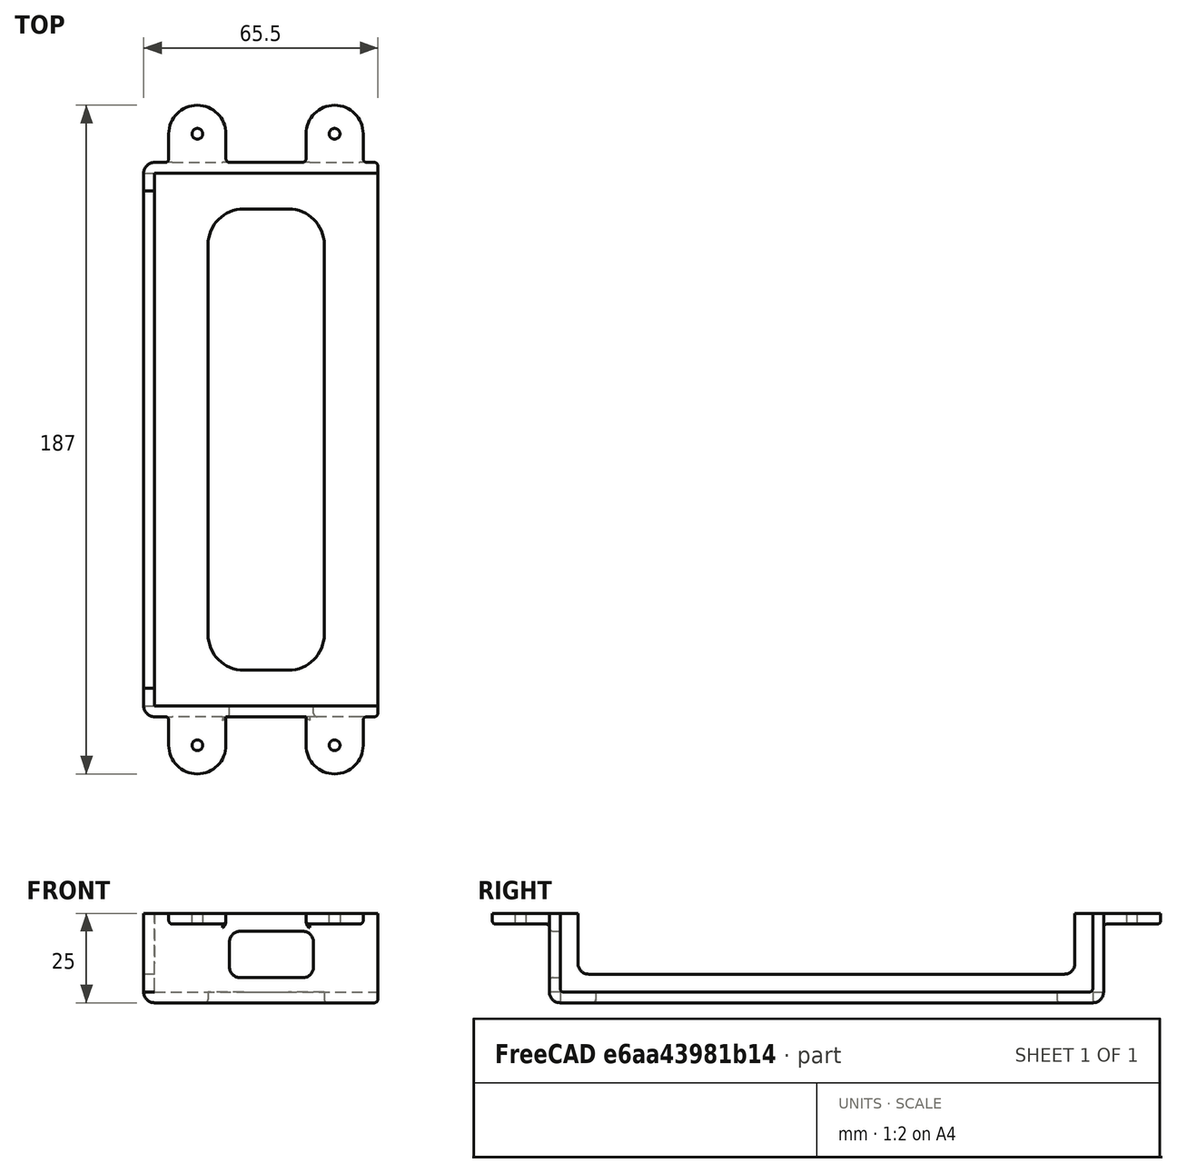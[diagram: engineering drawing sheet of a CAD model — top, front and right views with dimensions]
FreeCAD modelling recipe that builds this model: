
FCSTD DOCUMENT  (FreeCAD 0.21R33668 +7 (Git))
Label: UnderTableBracket-3
License: All rights reserved
LicenseURL: http://en.wikipedia.org/wiki/All_rights_reserved
objects: Sketcher::SketchObject×4, PartDesign::Pocket×3, PartDesign::Fillet×2, Spreadsheet::Sheet×1, PartDesign::AdditiveBox×1, PartDesign::Thickness×1, PartDesign::Pad×1, PartDesign::LinearPattern×1, PartDesign::Plane×1, PartDesign::Mirrored×1, PartDesign::MultiTransform×1, PartDesign::Body×1, App::Part×1, Mesh::Feature×1
note: 25 computed .brp shape members not serialized (recipe doc carries the construction recipe); baked Part::Feature solids carry a one-line shape summary decoded from their .brp

FEATURE [Spreadsheet::Sheet] Spreadsheet
  cells = A1='Width; B1(Width)=149; A2='Height; B2(Height)=22; A3='Depth; B3(Depth)=62.5; A4='Screw Diameter; B4(ScrewDiameter)=3
FEATURE [PartDesign::AdditiveBox] Box
  AttacherType = Attacher::AttachEngine3D
  Height = 22
  Length = 62.5
  Width = 149
  expr: Height = Spreadsheet.Height
  expr: Length = Spreadsheet.Depth
  expr: Width = Spreadsheet.Width
FEATURE [PartDesign::Thickness] Thickness
  Base = -> Box [Face6,Face2]
  BaseFeature = -> Box
  Intersection = false
  Join = 0
  Mode = 0
  SupportTransform = false
  Value = 3
FEATURE [Sketcher::SketchObject] Sketch
  ExternalGeometry = -> [Thickness]
  FullyConstrained = false
  MapMode = 5
  Placement = pos=(0,0,0) rot=(0.57735,0.57735,0.57735;2.0944rad)
  Support = -> [Thickness]
  sketch-geometry (8):
    g0: LineSegment StartX=144 StartY=22 StartZ=0 EndX=144 EndY=8 EndZ=0
    g1: ArcOfCircle CenterX=141 CenterY=8 CenterZ=0 NormalX=0 NormalY=0 NormalZ=1 AngleXU=0 Radius=3 StartAngle=4.71239 EndAngle=6.28319
    g2: LineSegment StartX=141 StartY=5 StartZ=0 EndX=8 EndY=5 EndZ=0
    g3: ArcOfCircle CenterX=8 CenterY=8 CenterZ=0 NormalX=0 NormalY=0 NormalZ=1 AngleXU=0 Radius=3 StartAngle=3.14159 EndAngle=4.71239
    g4: LineSegment StartX=5 StartY=8 StartZ=0 EndX=5 EndY=22 EndZ=0
    g5: GeomPoint X=5 Y=35.516 Z=0
    g6: GeomPoint X=144 Y=5 Z=0
    g7: LineSegment StartX=5 StartY=22 StartZ=0 EndX=144 EndY=22 EndZ=0
  constraints (19):
    c: Tangent(g0,g1) = 1.5708
    c: Tangent(g1,g2) = 1.5708
    c: Tangent(g2,g3) = 1.5708
    c: Tangent(g3,g4) = 1.5708
    c: Horizontal(g2)
    c: Vertical(g0)
    c: Vertical(g4)
    c: Equal(g1,g3)
    c: PointOnObject(g5,g4)
    c: PointOnObject(g6,g0)
    c: PointOnObject(g6,g2)
    c: PointOnObject(g4,g-3)
    c: PointOnObject(g0,g-3)
    c: Radius(g3) = 3
    c: DistanceX(g-3,g4) = 5
    c: DistanceX(g0,g-3) = 5
    c: DistanceY(g-1,g2) = 5
    c: Coincident(g7,g4)
    c: Coincident(g7,g0)
FEATURE [PartDesign::Pocket] Pocket
  BaseFeature = -> Thickness
  Direction = (-1,0,0)
  Length = 5
  Length2 = 5
  Profile = -> Sketch
  ReferenceAxis = -> Sketch [N_Axis]
  Type = 1
FEATURE [Sketcher::SketchObject] Sketch001
  ExternalGeometry = -> [Pocket]
  FullyConstrained = true
  MapMode = 5
  Support = -> [Pocket]
  sketch-geometry (10):
    g0: ArcOfCircle CenterX=25 CenterY=129 CenterZ=0 NormalX=0 NormalY=0 NormalZ=1 AngleXU=0 Radius=10 StartAngle=1.5708 EndAngle=3.14159
    g1: LineSegment StartX=25 StartY=139 StartZ=0 EndX=37.5 EndY=139 EndZ=0
    g2: ArcOfCircle CenterX=37.5 CenterY=129 CenterZ=0 NormalX=0 NormalY=0 NormalZ=1 AngleXU=0 Radius=10 StartAngle=1.2e-14 EndAngle=1.5708
    g3: LineSegment StartX=47.5 StartY=129 StartZ=0 EndX=47.5 EndY=20 EndZ=0
    g4: ArcOfCircle CenterX=37.5 CenterY=20 CenterZ=0 NormalX=0 NormalY=0 NormalZ=1 AngleXU=0 Radius=10 StartAngle=4.71239 EndAngle=6.28319
    g5: LineSegment StartX=37.5 StartY=10 StartZ=0 EndX=25 EndY=10 EndZ=0
    g6: ArcOfCircle CenterX=25 CenterY=20 CenterZ=0 NormalX=0 NormalY=0 NormalZ=1 AngleXU=0 Radius=10 StartAngle=3.14159 EndAngle=4.71239
    g7: LineSegment StartX=15 StartY=20 StartZ=0 EndX=15 EndY=129 EndZ=0
    g8: GeomPoint X=15 Y=139 Z=0
    g9: GeomPoint X=47.5 Y=10 Z=0
  constraints (24):
    c: Tangent(g0,g1) = 1.5708
    c: Tangent(g1,g2) = 1.5708
    c: Tangent(g2,g3) = 1.5708
    c: Tangent(g3,g4) = 1.5708
    c: Tangent(g4,g5) = 1.5708
    c: Tangent(g5,g6) = 1.5708
    c: Tangent(g6,g7) = 1.5708
    c: Tangent(g7,g0) = 1.5708
    c: Horizontal(g1)
    c: Horizontal(g5)
    c: Vertical(g3)
    c: Vertical(g7)
    c: Equal(g0,g2)
    c: Equal(g2,g4)
    c: Equal(g4,g6)
    c: PointOnObject(g8,g1)
    c: PointOnObject(g8,g7)
    c: PointOnObject(g9,g3)
    c: PointOnObject(g9,g5)
    c: Radius(g2) = 10
    c: DistanceY(g1,g-4) = 10
    c: DistanceY(g-4,g4) = 10
    c: DistanceX(g3,g-4) = 15
    c: DistanceX(g-3,g0) = 15
FEATURE [PartDesign::Pocket] Pocket001
  BaseFeature = -> Pocket
  Direction = (0,0,-1)
  Length = 5
  Length2 = 5
  Profile = -> Sketch001
  ReferenceAxis = -> Sketch001 [N_Axis]
  Type = 1
FEATURE [PartDesign::Fillet] Fillet
  Base = -> Pocket001 [Edge32,Edge34]
  BaseFeature = -> Pocket001
  Radius = 1
  SupportTransform = false
  UseAllEdges = false
FEATURE [Sketcher::SketchObject] Sketch002
  ExternalGeometry = -> [Box]
  FullyConstrained = true
  MapMode = 5
  Placement = pos=(0,0,22) rot=(0,0,1;0rad)
  Support = -> [Box]
  expr: Constraints[10] = Spreadsheet.ScrewDiameter
  sketch-geometry (5):
    g0: ArcOfCircle CenterX=12 CenterY=160 CenterZ=0 NormalX=0 NormalY=0 NormalZ=1 AngleXU=0 Radius=8 StartAngle=1.7e-15 EndAngle=3.14159
    g1: LineSegment StartX=4 StartY=160 StartZ=0 EndX=4 EndY=149 EndZ=0
    g2: LineSegment StartX=20 StartY=149 StartZ=0 EndX=20 EndY=160 EndZ=0
    g3: Circle CenterX=12 CenterY=160 CenterZ=0 NormalX=0 NormalY=0 NormalZ=1 AngleXU=0 Radius=1.5
    g4: LineSegment StartX=4 StartY=149 StartZ=0 EndX=20 EndY=149 EndZ=0
  constraints (13):
    c: Tangent(g0,g1) = -1.5708
    c: Tangent(g2,g0) = -1.5708
    c: Vertical(g1)
    c: PointOnObject(g1,g-3)
    c: PointOnObject(g2,g-3)
    c: Radius(g0) = 8
    c: Vertical(g2)
    c: DistanceY(g2,g2) = 11
    c: DistanceX(g-3,g1) = 4
    c: Coincident(g3,g0)
    c: Diameter(g3) = 3
    c: Coincident(g4,g1)
    c: Coincident(g4,g2)
FEATURE [PartDesign::Pad] Pad
  BaseFeature = -> Fillet
  Direction = (0,0,1)
  Length = 3
  Length2 = 10
  Profile = -> Sketch002
  ReferenceAxis = -> Sketch002 [N_Axis]
  Reversed = true
  Type = 0
FEATURE [PartDesign::LinearPattern] LinearPattern
  Direction = -> Sketch002 [H_Axis]
  Length = 38.4
  Occurrences = 2
FEATURE [PartDesign::Plane] DatumPlane
  AttachmentOffset = pos=(0,0,0) rot=(-0.57735,0.57735,0.57735;2.0944rad)
  Length = 63.2288
  MapMode = 45
  Placement = pos=(31.25,74.5,11) rot=(-0.57735,0.57735,0.57735;2.0944rad)
  ResizeMode = 0
  Support = -> [Box]
  Width = 100.729
FEATURE [PartDesign::Mirrored] Mirrored
  MirrorPlane = -> DatumPlane
FEATURE [PartDesign::MultiTransform] MultiTransform
  BaseFeature = -> Pad
  Originals = -> [Pad]
  Transformations = -> [LinearPattern,Mirrored]
FEATURE [Sketcher::SketchObject] Sketch003
  ExternalGeometry = -> [MultiTransform]
  FullyConstrained = true
  MapMode = 5
  Placement = pos=(0,-3,0) rot=(1,0,0;1.5708rad)
  Support = -> [MultiTransform]
  sketch-geometry (10):
    g0: ArcOfCircle CenterX=24 CenterY=14 CenterZ=0 NormalX=0 NormalY=0 NormalZ=1 AngleXU=0 Radius=3 StartAngle=1.5708 EndAngle=3.14159
    g1: LineSegment StartX=24 StartY=17 StartZ=0 EndX=41.5 EndY=17 EndZ=0
    g2: ArcOfCircle CenterX=41.5 CenterY=14 CenterZ=0 NormalX=0 NormalY=0 NormalZ=1 AngleXU=0 Radius=3 StartAngle=1e-16 EndAngle=1.5708
    g3: LineSegment StartX=44.5 StartY=14 StartZ=0 EndX=44.5 EndY=7 EndZ=0
    g4: ArcOfCircle CenterX=41.5 CenterY=7 CenterZ=0 NormalX=0 NormalY=0 NormalZ=1 AngleXU=0 Radius=3 StartAngle=4.71239 EndAngle=6.28319
    g5: LineSegment StartX=41.5 StartY=4 StartZ=0 EndX=24 EndY=4 EndZ=0
    g6: ArcOfCircle CenterX=24 CenterY=7 CenterZ=0 NormalX=0 NormalY=0 NormalZ=1 AngleXU=0 Radius=3 StartAngle=3.14159 EndAngle=4.71239
    g7: LineSegment StartX=21 StartY=7 StartZ=0 EndX=21 EndY=14 EndZ=0
    g8: GeomPoint X=21 Y=17 Z=0
    g9: GeomPoint X=44.5 Y=4 Z=0
  constraints (24):
    c: Tangent(g0,g1) = 1.5708
    c: Tangent(g1,g2) = 1.5708
    c: Tangent(g2,g3) = 1.5708
    c: Tangent(g3,g4) = 1.5708
    c: Tangent(g4,g5) = 1.5708
    c: Tangent(g5,g6) = 1.5708
    c: Tangent(g6,g7) = 1.5708
    c: Tangent(g7,g0) = 1.5708
    c: Horizontal(g1)
    c: Horizontal(g5)
    c: Vertical(g3)
    c: Vertical(g7)
    c: Equal(g0,g2)
    c: Equal(g2,g4)
    c: Equal(g4,g6)
    c: PointOnObject(g8,g1)
    c: PointOnObject(g8,g7)
    c: PointOnObject(g9,g3)
    c: PointOnObject(g9,g5)
    c: DistanceY(g1,g-3) = 5
    c: DistanceY(g-1,g5) = 4
    c: DistanceX(g-1,g6) = 21
    c: DistanceX(g2,g-3) = 18
    c: Radius(g0) = 3
FEATURE [PartDesign::Pocket] Pocket002
  BaseFeature = -> MultiTransform
  Direction = (0,1,-2e-16)
  Length = 5
  Length2 = 5
  Profile = -> Sketch003
  ReferenceAxis = -> Sketch003 [N_Axis]
  Type = 0
FEATURE [PartDesign::Fillet] Fillet001
  Base = -> Pocket002 [Edge138,Edge140,Edge125,Edge136,Edge134,Edge132,Edge130,Edge128,Edge182,Edge188,Edge187,Edge190,Edge191,Edge186,Edge144,Edge145,Edge81,Edge80,Edge78,Edge77,Edge76,Edge100,Edge170,Edge171,Edge169,Edge97,Edge162,Edge163,Edge161,Edge98,Edge95,Edge96,Edge99,Edge146,Edge147,Edge105,Edge108,Edge109,Edge112,Edge113,+3 more]
  BaseFeature = -> Pocket002
  Radius = 1
  SupportTransform = false
  UseAllEdges = false
FEATURE [PartDesign::Body] Body
  Group = -> [Box,Thickness,Sketch,Pocket,Sketch001,Pocket001,Fillet,Sketch002,Pad,MultiTransform,LinearPattern,DatumPlane,Mirrored,Sketch003,Pocket002,Fillet001]
  Origin = -> Origin001
  Tip = -> Fillet001
FEATURE [App::Part] Part  label="Bracket"
  Group = -> [Body]
  Origin = -> Origin
FEATURE [Mesh::Feature] Mesh  label="Bracket (Meshed)"
